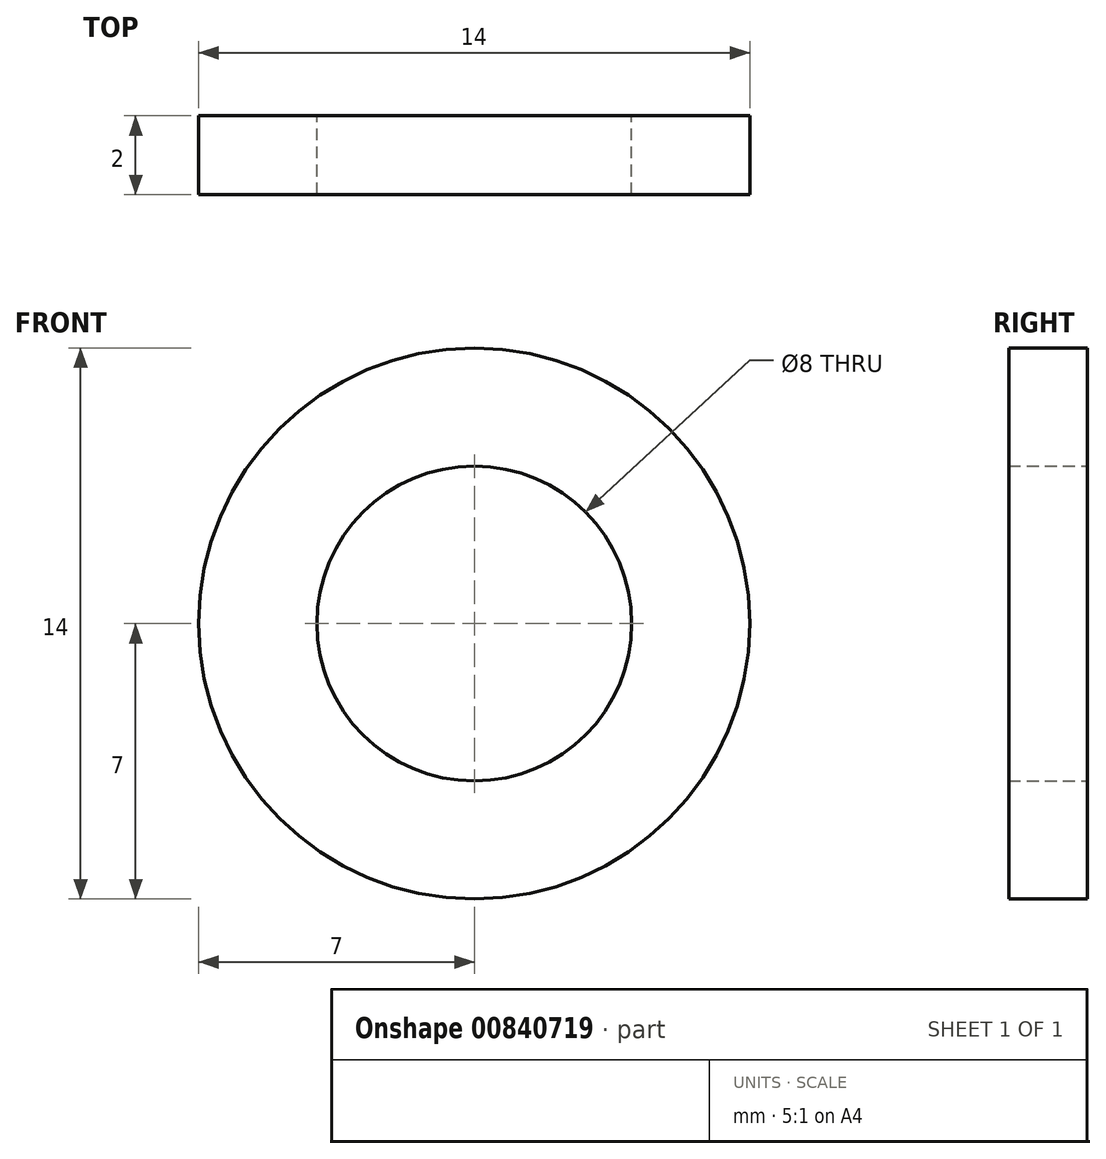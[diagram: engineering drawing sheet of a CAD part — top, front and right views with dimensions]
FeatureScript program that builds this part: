
annotation { "Feature Type Name" : "Feature", "Feature Type Description" : "" }
export const myFeature = defineFeature(function(context is Context, id is Id, definition is map)
    precondition{}
    {
        {
            var Q0;
            Q0=qCreatedBy(makeId("Front.planeOp"),FACE);
            var sketch = newSketch(context, id + "F0", { "sketchPlane" : qUnion([Q0])});
            skCircle(sketch, "E0", {"center": v(0, 0) * mm, "radius": 7 * mm});
            skCircle(sketch, "E1", {"center": v(0, 0) * mm, "radius": 4 * mm});
            skSolve(sketch);
        }
        {
            var Q0;
            Q0 = qSketchRegion(id + "F0", true);
            extrude(context, id + "F1", {"entities" : qUnion([Q0]), "depth" : 2 * mm, "offsetDistance" : 25 * mm});
        }
    });
